# Revit family: QF_T&S_B-0200-LN
name_source: partatom
category: Specialty Equipment
revit_build: Autodesk Revit Architecture 2012 (Build: 20110916_2132(x64)
units: mm (PartAtom-declared; Revit-internal decimal feet)

## types (1)
- QF_T&S_B-0200-LN
    Cold Water Connection Height = 0"
    Cold Water Consumption = 8.270 GPM
    Cold Water Inlet Flow = 8.27 GPM
    Cold Water Maximum Pressure = 125.00 psi
    Cold Water Minimum Pressure = 20.00 psi
    Cold Water Size = 1"
    Connector 1 Description = Cold Water Inlet
    Connector 2 Description = Hot Water Inlet
    Description = Single Hole Deck Mount Mixing Faucet With Polished Chrome Plated Brass Body, Swivel Outlet (Less Nozzle), Compression Cartridges, Lever Handles, And 18'' Flexible Stainelss Steel Supply Hoses With 1/2'' NPSM / 5/8'' O.D. Compression Connections
    Faucet Material = Metal-T&S Brass-Chrome Plated Brass
    Hot Water Connection Height = 0"
    Hot Water Consumption = 8.27 GPM
    Hot Water Inlet Flow = 8.27 GPM
    Hot Water Maximum Pressure = 125.00 psi
    Hot Water Minimum Pressure = 20.00 psi
    Hot Water Size = 1"
    Manufacturer = T&S Brass and Bronze Works, Inc.
    Model = B-0200-LN
    Product Documentation Link = http://catalog.tsbrass.com
    URL = http://www.tsbrass.com
    Water Supply Radius = 1/4"
    Weight in Pounds = 0

## geometry (parser evidence)
native form markers: Blend x14, Sweep x9
no freeform markers — native parametric forms only
